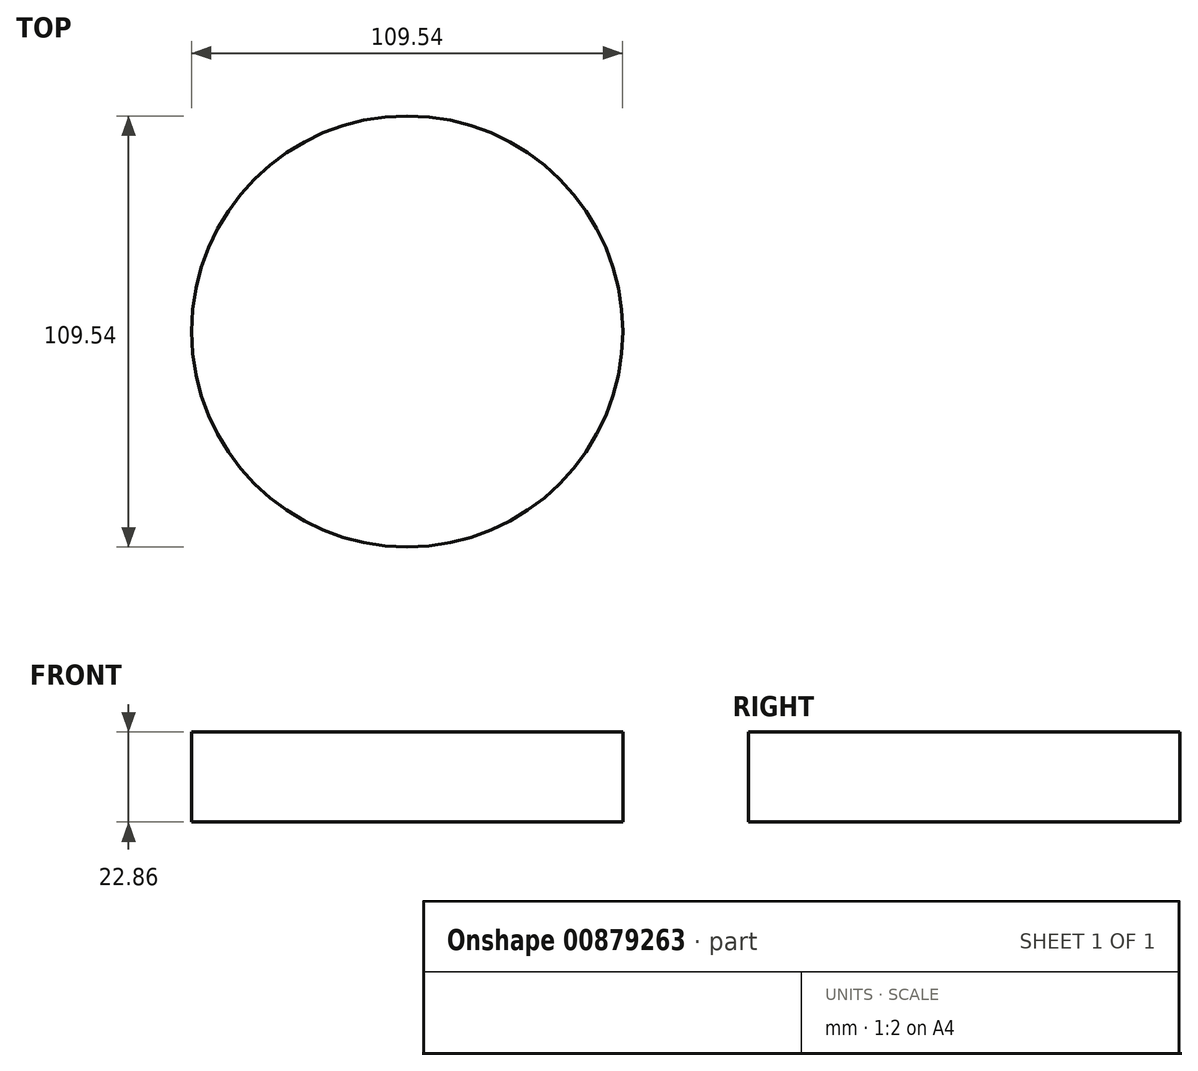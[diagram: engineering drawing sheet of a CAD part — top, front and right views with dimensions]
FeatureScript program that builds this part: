
annotation { "Feature Type Name" : "Feature", "Feature Type Description" : "" }
export const myFeature = defineFeature(function(context is Context, id is Id, definition is map)
    precondition{}
    {
        {
            var Q0;
            Q0=qCreatedBy(makeId("Top.planeOp"),FACE);
            var sketch = newSketch(context, id + "F0", { "sketchPlane" : qUnion([Q0])});
            skLineSegment(sketch, "E0", {"start": v(139.22, 59.63) * mm, "end": v(139.26, 59.63) * mm});
            skLineSegment(sketch, "E1", {"start": v(139.26, 59.63) * mm, "end": v(139.22, 59.63) * mm});
            skLineSegment(sketch, "E2", {"start": v(84.48, 28) * mm, "end": v(84.45, 27.95) * mm});
            skLineSegment(sketch, "E3", {"start": v(84.45, 27.95) * mm, "end": v(84.48, 28) * mm});
            skCircle(sketch, "E4", {"center": v(102.7, 59.63) * mm, "radius": 36.51 * mm});
            skPoint(sketch, "E5.orphan", {"position": v(108.19, 62.8) * mm});
            skPoint(sketch, "E6.orphan", {"position": v(102.7, 53.73) * mm});
            skPoint(sketch, "E7.orphan", {"position": v(108.19, 56.47) * mm});
            skPoint(sketch, "E8.orphan", {"position": v(97.23, 56.47) * mm});
            skPoint(sketch, "E9.orphan", {"position": v(84.44, 91.23) * mm});
            skPoint(sketch, "E10.end.orphan", {"position": v(120.97, 91.2) * mm});
            skPoint(sketch, "E11.end.orphan", {"position": v(120.97, 28.04) * mm});
            skSolve(sketch);
        }
        {
            var Q0;
            {var subQ0=sQuery(id+"F0.wireOp",EDGE,"E4");var subQ1=makeQuery(id+"F0.imprint","IMPRINT",VERTEX,{"disambiguationData":[OD(0.0)],"derivedFrom":subQ0});Q0=makeQuery(id+"F0.imprint","IMPRINT",FACE,{"disambiguationData":[TD([[makeQuery(id+"F0.imprint","IMPRINT",EDGE,{"disambiguationData":[TD([[subQ1,-1.0]])],"derivedFrom":subQ0}),1.0]])]});}
            extrude(context, id + "F1", {"entities" : qUnion([Q0]), "depth" : 15.24 * mm, "offsetDistance" : 25.4 * mm});
        }
        {
            var Q0;
            Q0=makeQuery(id+"F1.opExtrude","SWEPT_BODY",BODY,{"disambiguationData":[OSD([sQuery(id+"F0.wireOp",EDGE,"E4")])]});
            var Q1;
            Q1=qCreatedBy(makeId("Origin.pointOp"),VERTEX);
            transform(context, id + "F2", {"entities" : qUnion([Q0]), "transformType" : TransformType.SCALE_UNIFORMLY, "scale" : 1.5, "scalePoint" : qUnion([Q1]), "makeCopy" : false});
        }
    });
